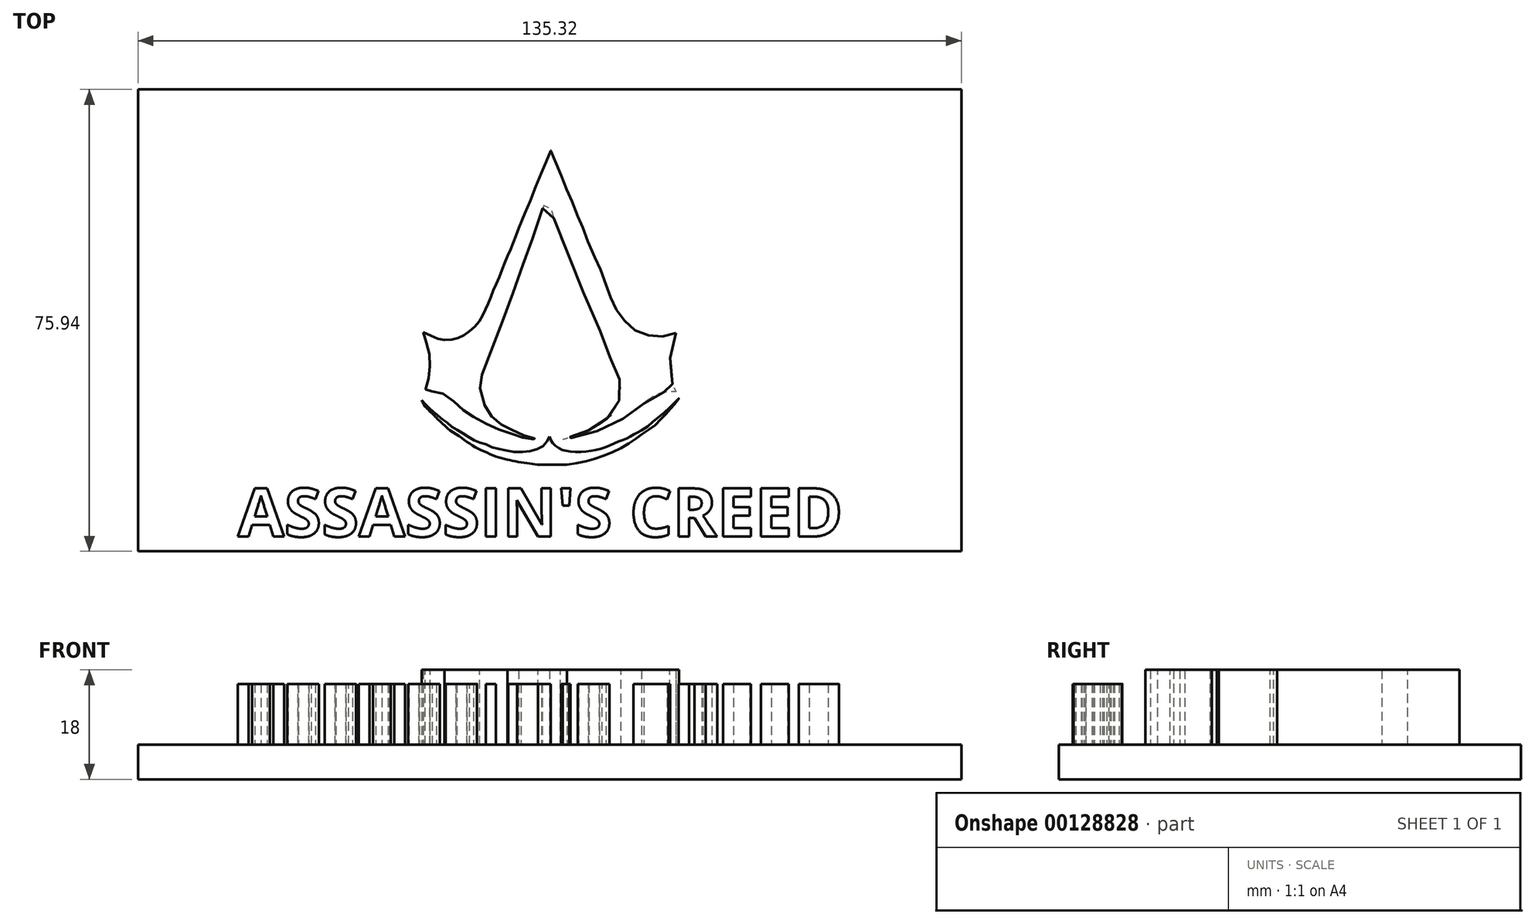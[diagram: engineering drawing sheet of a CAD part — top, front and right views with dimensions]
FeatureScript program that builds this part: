
annotation { "Feature Type Name" : "Feature", "Feature Type Description" : "" }
export const myFeature = defineFeature(function(context is Context, id is Id, definition is map)
    precondition{}
    {
        {
            var Q0;
            Q0=qCreatedBy(makeId("Top.planeOp"),FACE);
            var sketch = newSketch(context, id + "F0", { "sketchPlane" : qUnion([Q0])});
            skLineSegment(sketch, "E0.bottom", {"start": v(-69.34, 33.59) * mm, "end": v(72.51, 33.59) * mm});
            skLineSegment(sketch, "E0.top", {"start": v(-69.34, -35.9) * mm, "end": v(72.51, -35.9) * mm});
            skLineSegment(sketch, "E0.left", {"start": v(-69.34, 33.59) * mm, "end": v(-69.34, -35.9) * mm});
            skLineSegment(sketch, "E0.right", {"start": v(72.51, 33.59) * mm, "end": v(72.51, -35.9) * mm});
            skFitSpline(sketch, "E1", {"points": [v(-21.04, -2.8) * mm, v(-19.03, -3.68) * mm, v(-17.47, -4.05) * mm, v(-15.84, -3.86) * mm, v(-14.65, -3.49) * mm, v(-13.33, -2.49) * mm, v(-12.2, -1.55) * mm, v(-11.27, 0) * mm, v(-10.7, 1.15) * mm, v(-10.08, 2.59) * mm, v(-9.51, 4.1) * mm, v(-8.82, 5.66) * mm, v(-8.07, 7.54) * mm, v(-7.45, 9.16) * mm, v(-6.7, 10.8) * mm, v(-6.07, 12.48) * mm, v(-5.32, 14.3) * mm], "startDerivative": vector(29.02, -13.4) * mm, "endDerivative": vector(11.72, 27.06) * mm});
            skPoint(sketch, "E2.7.internal.snap0", {"position": v(-0.43, 27.1) * mm});
            skFitSpline(sketch, "E2", {"points": [v(-5.32, 14.3) * mm, v(-4.3, 16.82) * mm, v(-3.56, 18.57) * mm, v(-2.73, 20.68) * mm, v(-1.82, 22.97) * mm, v(-1.11, 24.63) * mm, v(-0.62, 25.88) * mm, v(0, 27.1) * mm, v(0.78, 25.08) * mm, v(1.49, 23.44) * mm, v(2.3, 21.34) * mm, v(3.06, 19.58) * mm, v(3.83, 17.75) * mm, v(4.83, 15.16) * mm, v(5.25, 14.3) * mm, v(6.07, 11.92) * mm, v(7.3, 9.2) * mm, v(8.08, 7.54) * mm, v(8.96, 5.08) * mm, v(9.67, 3.25) * mm, v(10.44, 1.36) * mm, v(11.44, 0) * mm, v(12.74, -1.65) * mm, v(14.5, -2.83) * mm, v(16.5, -3.36) * mm, v(18.51, -3.42) * mm, v(20.52, -2.89) * mm], "startDerivative": vector(23.45, 59.98) * mm, "endDerivative": vector(51.48, 17.17) * mm});
            skFitSpline(sketch, "E3", {"points": [v(20.52, -2.89) * mm, v(20.1, -4.58) * mm, v(19.69, -6.05) * mm, v(19.49, -7.97) * mm, v(19.59, -9.74) * mm, v(19.94, -11.35) * mm, v(20.52, -12.77) * mm, v(19.59, -12.52) * mm, v(18.51, -12.62) * mm, v(17.51, -12.92) * mm, v(16.15, -13.68) * mm, v(15.04, -14.7) * mm, v(13.82, -15.65) * mm, v(12.2, -16.76) * mm, v(10.44, -17.72) * mm, v(8.51, -18.63) * mm, v(6.75, -19.3) * mm, v(5.08, -19.75) * mm, v(3, -20.2) * mm, v(1.54, -20.5) * mm, v(2.1, -20.3) * mm, v(3, -20.05) * mm, v(3.76, -19.8) * mm, v(4.52, -19.6) * mm, v(5.53, -19.2) * mm, v(6.8, -18.53) * mm, v(7.55, -18.08) * mm, v(8.72, -17.32) * mm, v(9.58, -16.56) * mm, v(10.49, -15.55) * mm, v(11, -14.49) * mm, v(11.35, -13.33) * mm, v(11.45, -12.16) * mm, v(11.4, -11.25) * mm, v(10.94, -9.69) * mm, v(10.39, -8.42) * mm, v(9.73, -7) * mm, v(9.12, -5.34) * mm, v(8.46, -3.42) * mm, v(7.6, -1.8) * mm, v(6.85, 0) * mm, v(0.69, 15.18) * mm, v(0, 17.5) * mm, v(-0.85, 18.56) * mm, v(-1.64, 16.77) * mm, v(-2.59, 14.35) * mm, v(-3.22, 12.25) * mm, v(-3.96, 10.35) * mm, v(-4.59, 8.56) * mm, v(-5.32, 6.46) * mm, v(-6.11, 4.2) * mm, v(-6.95, 1.93) * mm, v(-7.7, 0) * mm, v(-8.48, -2.28) * mm, v(-9.06, -3.42) * mm, v(-9.74, -5.49) * mm, v(-10.7, -7.96) * mm, v(-11.37, -9.75) * mm], "startDerivative": vector(-23.55, -99.1) * mm, "endDerivative": vector(-34.74, -92.92) * mm});
            skFitSpline(sketch, "E4", {"points": [v(-11.37, -9.75) * mm, v(-11.72, -11.05) * mm, v(-11.37, -13.84) * mm, v(-10.46, -15.61) * mm, v(-9.7, -16.7) * mm, v(-8.57, -17.67) * mm, v(-7.64, -18.28) * mm, v(-6.43, -18.84) * mm, v(-5.22, -19.45) * mm, v(-3.93, -19.9) * mm, v(-2.96, -20.17) * mm, v(-2.2, -20.46) * mm, v(-2.76, -20.42) * mm, v(-3.44, -20.3) * mm, v(-4.37, -20.13) * mm, v(-5.46, -19.9) * mm, v(-6.71, -19.4) * mm, v(-8.16, -18.96) * mm, v(-9.66, -18.28) * mm, v(-11.37, -17.47) * mm, v(-12.89, -16.62) * mm, v(-13.9, -16.02) * mm, v(-15.07, -15.05) * mm, v(-16.11, -14.04) * mm, v(-17.33, -13.2) * mm, v(-18.54, -12.5) * mm, v(-19.63, -12.47) * mm, v(-20.68, -12.75) * mm, v(-20.6, -11.98) * mm, v(-20.27, -10.93) * mm, v(-20.07, -9.75) * mm, v(-19.95, -8.51) * mm, v(-19.9, -7.1) * mm, v(-20.11, -6) * mm, v(-20.4, -4.84) * mm, v(-20.8, -3.67) * mm, v(-21.04, -2.8) * mm], "startDerivative": vector(-15.26, -39.9) * mm, "endDerivative": vector(-8.88, 35.9) * mm});
            skFitSpline(sketch, "E5", {"points": [v(-21.85, -13.5) * mm, v(-21.36, -13.9) * mm, v(-20.72, -14.6) * mm, v(-20.05, -15.23) * mm, v(-19.5, -15.74) * mm, v(-18.77, -16.35) * mm, v(-17.88, -17.15) * mm, v(-17.05, -17.7) * mm, v(-16.22, -18.42) * mm, v(-15.16, -19) * mm, v(-14.08, -19.7) * mm, v(-12.96, -20.37) * mm, v(-11.87, -20.85) * mm, v(-10.85, -21.17) * mm, v(-9.6, -21.71) * mm, v(-8.3, -22.03) * mm, v(-6.38, -22.42) * mm, v(-4.44, -22.45) * mm, v(-2.8, -22.16) * mm, v(-1.47, -21.55) * mm, v(-0.73, -20.82) * mm, v(-0.25, -19.9) * mm], "startDerivative": vector(14.24, -9.7) * mm, "endDerivative": vector(9.72, 21.63) * mm});
            skFitSpline(sketch, "E6", {"points": [v(-0.25, -19.9) * mm, v(0, -20.65) * mm, v(0.46, -21.26) * mm, v(1.22, -21.84) * mm, v(2.1, -22.2) * mm, v(3, -22.35) * mm, v(4.43, -22.48) * mm, v(6.07, -22.35) * mm, v(7.3, -22.15) * mm, v(8.77, -21.74) * mm, v(9.94, -21.26) * mm, v(11.16, -20.72) * mm, v(12.26, -20.3) * mm, v(13.02, -19.9) * mm, v(14.06, -19.3) * mm, v(14.82, -18.92) * mm], "startDerivative": vector(3.73, -13.92) * mm, "endDerivative": vector(12.38, 5.93) * mm});
            skFitSpline(sketch, "E7", {"points": [v(14.82, -18.92) * mm, v(15.65, -18.38) * mm, v(16.32, -17.88) * mm, v(16.98, -17.27) * mm, v(17.78, -16.64) * mm, v(18.52, -16) * mm, v(19.27, -15.34) * mm, v(19.93, -14.68) * mm, v(20.68, -13.96) * mm, v(21, -13.63) * mm, v(20.54, -14.3) * mm, v(20.1, -14.9) * mm, v(19.55, -15.45) * mm, v(18.91, -16.11) * mm, v(18.33, -16.75) * mm, v(17.53, -17.58) * mm, v(16.67, -18.38) * mm, v(15.8, -18.92) * mm, v(14.82, -19.6) * mm, v(13.97, -20.26) * mm, v(12.9, -20.97) * mm, v(11.65, -21.7) * mm, v(10.16, -22.44) * mm, v(8.58, -23.1) * mm, v(7.17, -23.57) * mm, v(5.99, -23.93) * mm, v(4.27, -24.29) * mm, v(2.62, -24.53) * mm], "startDerivative": vector(24.25, 15.45) * mm, "endDerivative": vector(-35.52, -4.62) * mm});
            skFitSpline(sketch, "E8", {"points": [v(2.62, -24.53) * mm, v(1.3, -24.53) * mm, v(0.35, -24.53) * mm, v(-0.66, -24.53) * mm, v(-1.47, -24.53) * mm, v(-2.4, -24.53) * mm, v(-3.37, -24.36) * mm, v(-4.64, -24.22) * mm, v(-6.1, -23.97) * mm, v(-7.2, -23.7) * mm], "startDerivative": vector(-11.24, 0) * mm, "endDerivative": vector(-9.3, 2.39) * mm});
            skFitSpline(sketch, "E9", {"points": [v(-7.2, -23.7) * mm, v(-8.69, -23.35) * mm, v(-10.2, -22.74) * mm, v(-11.79, -22.03) * mm, v(-13.63, -20.96) * mm, v(-15, -19.97) * mm, v(-16.82, -18.75) * mm, v(-17.56, -18.07) * mm], "startDerivative": vector(-11, 2.13) * mm, "endDerivative": vector(-5.59, 5.77) * mm});
            skFitSpline(sketch, "E10", {"points": [v(-17.56, -18.07) * mm, v(-18.58, -17.15) * mm, v(-19.35, -16.35) * mm, v(-20.39, -15.33) * mm, v(-20.91, -14.73) * mm, v(-21.3, -13.94) * mm, v(-21.85, -13.5) * mm], "startDerivative": vector(-5.63, 4.9) * mm, "endDerivative": vector(-3.92, 3.04) * mm});
            skSolve(sketch);
        }
        {
            var Q0;
            Q0=makeQuery(id+"F0.imprint","IMPRINT",FACE,{"disambiguationData":[TD([[makeQuery(id+"F0.imprint","IMPRINT",EDGE,{"derivedFrom":sQuery(id+"F0.wireOp",EDGE,"E1")}),-1.0]])]});
            extrude(context, id + "F1", {"entities" : qUnion([Q0]), "depth" : 18 * mm});
        }
        {
            var Q0;
            {var subQ0=sQuery(id+"F0.wireOp",EDGE,"E6");Q0=makeQuery(id+"F0.imprint","IMPRINT",FACE,{"disambiguationData":[TD([[makeQuery(id+"F0.imprint","IMPRINT",EDGE,{"derivedFrom":subQ0}),-1.0]])]});}
            extrude(context, id + "F2", {"entities" : qUnion([Q0]), "depth" : 18 * mm});
        }
        {
            var Q0;
            Q0=qCreatedBy(makeId("Top.planeOp"),FACE);
            var sketch = newSketch(context, id + "F3", { "sketchPlane" : qUnion([Q0])});
            skLineSegment(sketch, "E11.bottom", {"start": v(-67.9, 37.16) * mm, "end": v(67.41, 37.16) * mm});
            skLineSegment(sketch, "E11.top", {"start": v(-67.9, -38.78) * mm, "end": v(67.41, -38.78) * mm});
            skLineSegment(sketch, "E11.left", {"start": v(-67.9, 37.16) * mm, "end": v(-67.9, -38.78) * mm});
            skLineSegment(sketch, "E11.right", {"start": v(67.41, 37.16) * mm, "end": v(67.41, -38.78) * mm});
            skSolve(sketch);
        }
        {
            var Q0;
            Q0=makeQuery(id+"F3.imprint","IMPRINT",FACE,{"disambiguationData":[TD([[makeQuery(id+"F3.imprint","IMPRINT",EDGE,{"derivedFrom":sQuery(id+"F3.wireOp",EDGE,"E11.bottom")}),-1.0]])]});
            extrude(context, id + "F4", {"entities" : qUnion([Q0]), "operationType" : NewBodyOperationType.ADD, "depth" : 5.67 * mm});
        }
        {
            var Q0;
            Q0=makeQuery(id+"F4.opExtrude","CAP_FACE",FACE,{"disambiguationData":[OSD([sQuery(id+"F3.wireOp",EDGE,"E11.bottom"),sQuery(id+"F3.wireOp",EDGE,"E11.top"),sQuery(id+"F3.wireOp",EDGE,"E11.left"),sQuery(id+"F3.wireOp",EDGE,"E11.right")])],"isStart":false});
            var sketch = newSketch(context, id + "F5", { "sketchPlane" : qUnion([Q0])});
            skText(sketch, "E12", { "text": "ASSASSIN\'S CREED\n", "fontName": "OpenSans-Bold.ttf"});
            const initialGuessF5  = {"E12": [-0.05153, -0.03637, 1, 0, 0.00799]};
            skSetInitialGuess(sketch, initialGuessF5);
            skSolve(sketch);
        }
        {
            var Q0;
            Q0 = qSketchRegion(id + "F5", true);
            extrude(context, id + "F6", {"entities" : qUnion([Q0]), "operationType" : NewBodyOperationType.ADD, "depth" : 10 * mm});
        }
    });
